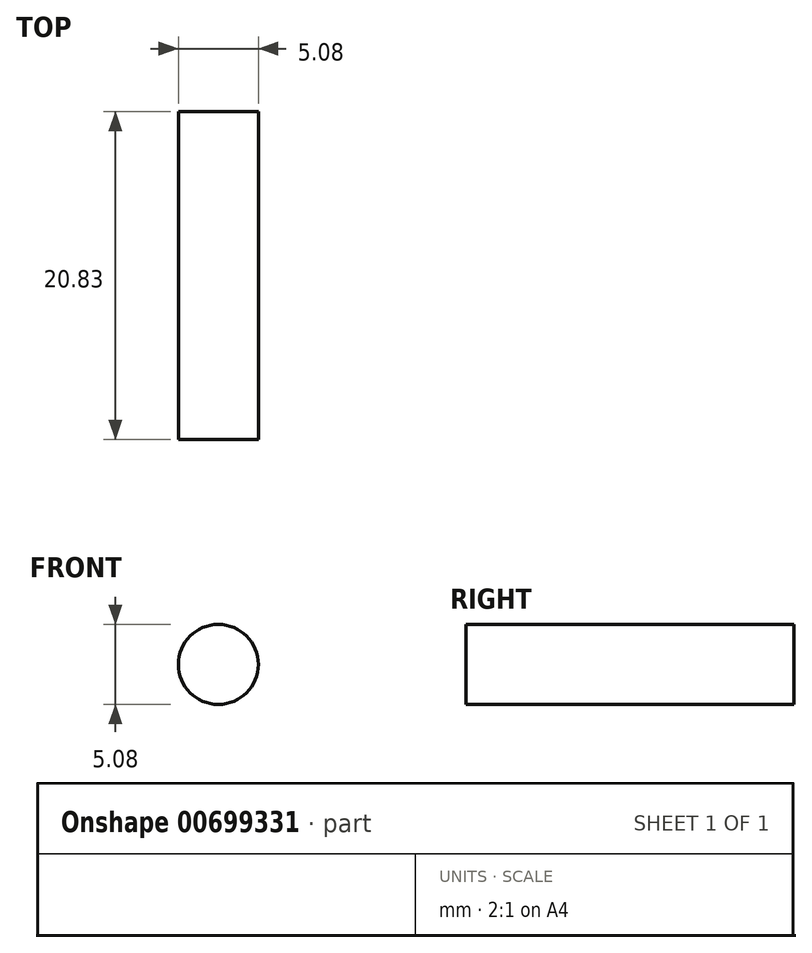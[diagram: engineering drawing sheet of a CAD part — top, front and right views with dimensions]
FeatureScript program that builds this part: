
annotation { "Feature Type Name" : "Feature", "Feature Type Description" : "" }
export const myFeature = defineFeature(function(context is Context, id is Id, definition is map)
    precondition{}
    {
        {
            var Q0;
            Q0=qCreatedBy(makeId("Front.planeOp"),FACE);
            var sketch = newSketch(context, id + "F0", { "sketchPlane" : qUnion([Q0])});
            skCircle(sketch, "E0", {"center": v(0, 0) * mm, "radius": 2.54 * mm});
            skSolve(sketch);
        }
        {
            var Q0;
            Q0=makeQuery(id+"F0.imprint","IMPRINT",FACE,{"disambiguationData":[TD([[makeQuery(id+"F0.imprint","IMPRINT",EDGE,{"derivedFrom":sQuery(id+"F0.wireOp",EDGE,"E0")}),1.0]])]});
            extrude(context, id + "F1", {"entities" : qUnion([Q0]), "depth" : 20.83 * mm, "offsetDistance" : 25.4 * mm});
        }
    });
